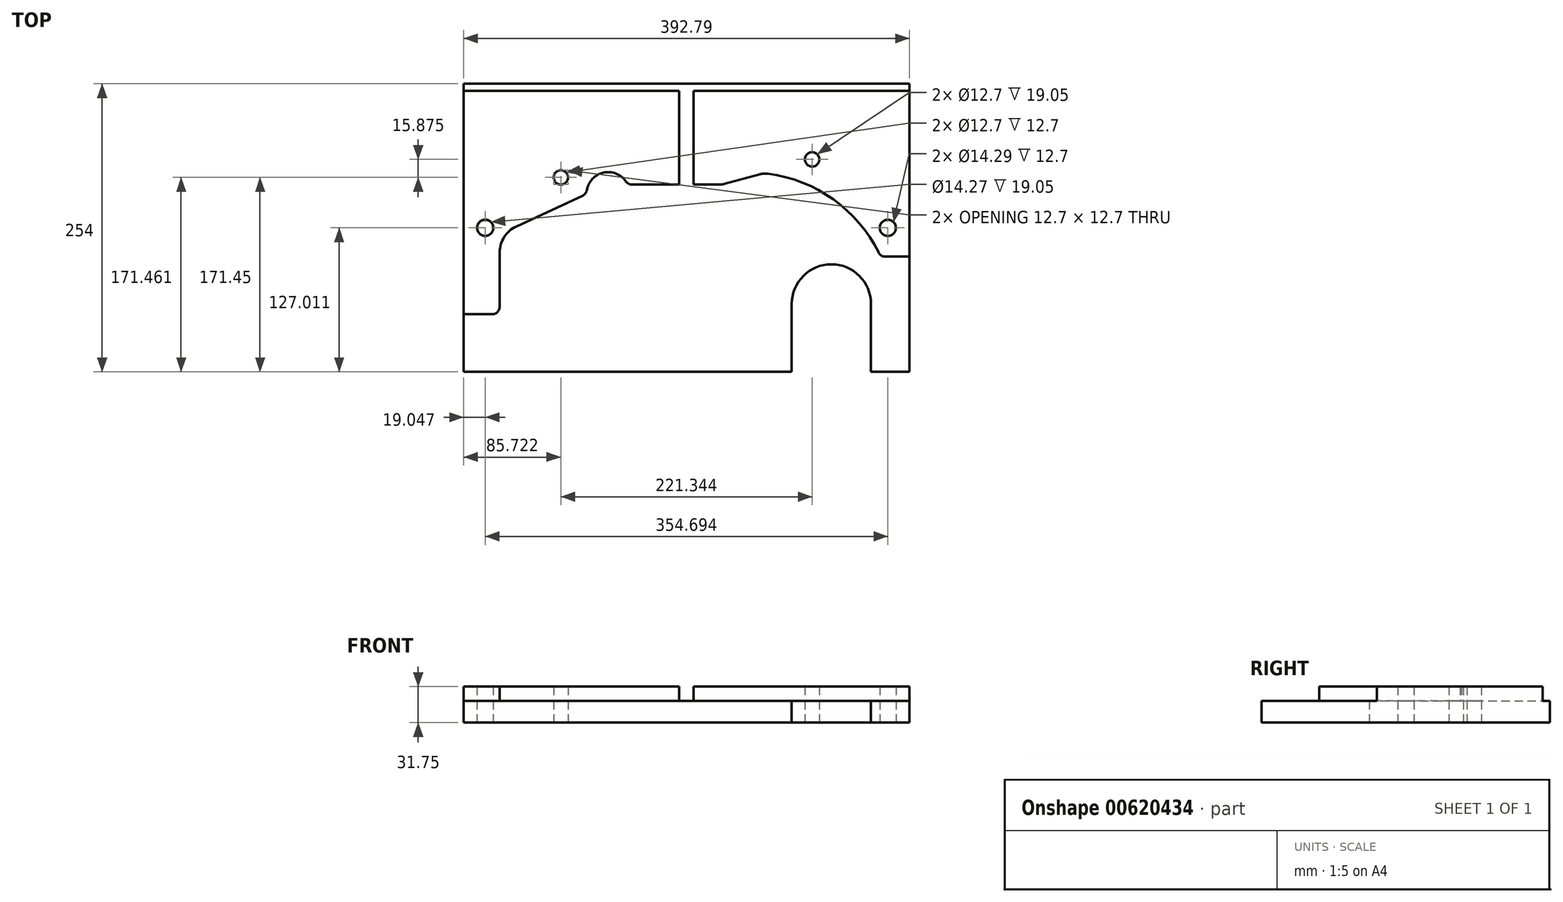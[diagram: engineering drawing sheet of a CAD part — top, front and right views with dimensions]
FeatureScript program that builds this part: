
annotation { "Feature Type Name" : "Feature", "Feature Type Description" : "" }
export const myFeature = defineFeature(function(context is Context, id is Id, definition is map)
    precondition{}
    {
        {
            var Q0;
            Q0=qCreatedBy(makeId("Top.planeOp"),FACE);
            var sketch = newSketch(context, id + "F0", { "sketchPlane" : qUnion([Q0])});
            skLineSegment(sketch, "E0", {"start": v(153.35, -127) * mm, "end": v(-112.4, -127) * mm});
            skArc(sketch, "E1", {"start": v(-112.4, -127) * mm, "mid": v(-149.75, -68.16) * mm, "end": v(-187.1, -127) * mm});
            skLineSegment(sketch, "E2", {"start": v(-187.1, -127) * mm, "end": v(-239.44, -127) * mm});
            skLineSegment(sketch, "E3", {"start": v(-239.44, -127) * mm, "end": v(-239.44, 127) * mm});
            skLineSegment(sketch, "E4", {"start": v(-239.44, 127) * mm, "end": v(153.35, 127) * mm});
            skLineSegment(sketch, "E5", {"start": v(153.35, 127) * mm, "end": v(153.35, -127) * mm});
            skCircle(sketch, "E6", {"center": v(-153.72, 44.45) * mm, "radius": 6.35 * mm});
            skCircle(sketch, "E7", {"center": v(67.63, 60.33) * mm, "radius": 6.35 * mm});
            skCircle(sketch, "E8", {"center": v(-220.4, 0) * mm, "radius": 7.14 * mm});
            skCircle(sketch, "E9", {"center": v(134.3, 0) * mm, "radius": 7.14 * mm});
            skCircle(sketch, "E10", {"center": v(84.58, -67.07) * mm, "radius": 34.93 * mm});
            skSolve(sketch);
        }
        {
            var Q0;
            Q0=qSketchRegion(id+"F0",true);
            extrude(context, id + "F1", {"entities" : qUnion([Q0]), "depth" : 19.05 * mm, "offsetDistance" : 25.4 * mm});
        }
        {
            var Q0;
            Q0=makeQuery(id+"F1.opExtrude","CAP_FACE",FACE,{"disambiguationData":[OSD([sQuery(id+"F0.wireOp",EDGE,"E0"),sQuery(id+"F0.wireOp",EDGE,"E1"),sQuery(id+"F0.wireOp",EDGE,"E2"),sQuery(id+"F0.wireOp",EDGE,"E3"),sQuery(id+"F0.wireOp",EDGE,"E4"),sQuery(id+"F0.wireOp",EDGE,"E5"),sQuery(id+"F0.wireOp",EDGE,"E8"),sQuery(id+"F0.wireOp",EDGE,"E10"),sQuery(id+"F0.wireOp",EDGE,"E9"),sQuery(id+"F0.wireOp",EDGE,"E6"),sQuery(id+"F0.wireOp",EDGE,"E7")])],"isStart":false});
            var sketch = newSketch(context, id + "F2", { "sketchPlane" : qUnion([Q0])});
            skArc(sketch, "E11", {"start": v(-193.03, 1.2) * mm, "mid": v(-203.71, -8.17) * mm, "end": v(-207.7, -21.82) * mm});
            skArc(sketch, "E12", {"start": v(28.82, 47.68) * mm, "mid": v(25.06, 47.8) * mm, "end": v(21.36, 47.17) * mm});
            skLineSegment(sketch, "E13", {"start": v(-9.42, 38.78) * mm, "end": v(21.36, 47.17) * mm});
            skArc(sketch, "E14", {"start": v(-14.43, 38.11) * mm, "mid": v(-11.9, 38.28) * mm, "end": v(-9.42, 38.78) * mm});
            skLineSegment(sketch, "E15", {"start": v(21.36, 47.17) * mm, "end": v(-9.42, 38.78) * mm});
            skArc(sketch, "E16", {"start": v(126.32, -21.97) * mm, "mid": v(86.3, 25.08) * mm, "end": v(28.82, 47.68) * mm});
            skCircle(sketch, "E17", {"center": v(-153.72, 44.46) * mm, "radius": 6.35 * mm});
            skCircle(sketch, "E18", {"center": v(67.63, 60.34) * mm, "radius": 6.35 * mm});
            skCircle(sketch, "E19", {"center": v(-220.4, 0.01) * mm, "radius": 7.14 * mm});
            skCircle(sketch, "E20", {"center": v(134.3, 0.01) * mm, "radius": 7.14 * mm});
            skLineSegment(sketch, "E21", {"start": v(-239.44, 120.66) * mm, "end": v(-49.4, 120.66) * mm});
            skLineSegment(sketch, "E22", {"start": v(-49.4, 120.66) * mm, "end": v(-239.44, 120.66) * mm});
            skLineSegment(sketch, "E23", {"start": v(-49.4, 120.66) * mm, "end": v(-49.4, 38.11) * mm});
            skLineSegment(sketch, "E24", {"start": v(-49.4, 38.11) * mm, "end": v(-49.4, 120.66) * mm});
            skLineSegment(sketch, "E25", {"start": v(-36.7, 38.11) * mm, "end": v(-36.7, 120.66) * mm});
            skLineSegment(sketch, "E26", {"start": v(-36.7, 120.66) * mm, "end": v(-36.7, 38.11) * mm});
            skLineSegment(sketch, "E27", {"start": v(-36.7, 120.66) * mm, "end": v(153.35, 120.66) * mm});
            skLineSegment(sketch, "E28", {"start": v(153.35, 120.66) * mm, "end": v(-36.7, 120.66) * mm});
            skLineSegment(sketch, "E29", {"start": v(-49.4, 38.11) * mm, "end": v(-91.17, 38.11) * mm});
            skLineSegment(sketch, "E30", {"start": v(-91.17, 38.11) * mm, "end": v(-49.4, 38.11) * mm});
            skLineSegment(sketch, "E31", {"start": v(-239.44, -76.19) * mm, "end": v(-239.44, 120.66) * mm});
            skLineSegment(sketch, "E32", {"start": v(-214.04, -76.19) * mm, "end": v(-239.44, -76.19) * mm});
            skArc(sketch, "E33", {"start": v(-214.04, -76.19) * mm, "mid": v(-209.55, -74.33) * mm, "end": v(-207.7, -69.84) * mm});
            skLineSegment(sketch, "E34", {"start": v(-207.7, -21.82) * mm, "end": v(-207.7, -69.84) * mm});
            skArc(sketch, "E35", {"start": v(-193.03, 1.2) * mm, "mid": v(-203.72, -8.17) * mm, "end": v(-207.7, -21.82) * mm});
            skLineSegment(sketch, "E36", {"start": v(-134.46, 28.51) * mm, "end": v(-193.03, 1.2) * mm});
            skArc(sketch, "E37", {"start": v(-134.46, 28.51) * mm, "mid": v(-132.09, 30.42) * mm, "end": v(-130.88, 33.22) * mm});
            skArc(sketch, "E38", {"start": v(-96.4, 40.86) * mm, "mid": v(-116.21, 48.66) * mm, "end": v(-130.88, 33.22) * mm});
            skArc(sketch, "E39", {"start": v(-96.4, 40.86) * mm, "mid": v(-94.12, 38.84) * mm, "end": v(-91.17, 38.11) * mm});
            skLineSegment(sketch, "E40", {"start": v(-239.44, -76.19) * mm, "end": v(-214.04, -76.19) * mm});
            skLineSegment(sketch, "E41", {"start": v(131.96, -25.39) * mm, "end": v(153.35, -25.39) * mm});
            skArc(sketch, "E42", {"start": v(126.27, -21.86) * mm, "mid": v(128.6, -24.44) * mm, "end": v(131.96, -25.39) * mm});
            skArc(sketch, "E43", {"start": v(126.27, -21.86) * mm, "mid": v(86.25, 25.12) * mm, "end": v(28.82, 47.68) * mm});
            skLineSegment(sketch, "E44", {"start": v(-36.7, 38.11) * mm, "end": v(-14.43, 38.11) * mm});
            skLineSegment(sketch, "E45", {"start": v(-193.03, 1.2) * mm, "end": v(-134.46, 28.51) * mm});
            skLineSegment(sketch, "E46", {"start": v(-207.7, -69.84) * mm, "end": v(-207.7, -21.82) * mm});
            skLineSegment(sketch, "E47", {"start": v(-239.44, 120.66) * mm, "end": v(-239.44, -76.19) * mm});
            skLineSegment(sketch, "E48", {"start": v(153.35, -25.39) * mm, "end": v(153.35, 120.66) * mm});
            skLineSegment(sketch, "E49", {"start": v(-14.43, 38.11) * mm, "end": v(-36.7, 38.11) * mm});
            skLineSegment(sketch, "E50", {"start": v(153.35, -25.39) * mm, "end": v(131.96, -25.39) * mm});
            skLineSegment(sketch, "E51", {"start": v(153.35, 120.66) * mm, "end": v(153.35, -25.39) * mm});
            skSolve(sketch);
        }
        {
            var Q0;
            Q0=qSketchRegion(id+"F2",true);
            extrude(context, id + "F3", {"entities" : qUnion([Q0]), "operationType" : NewBodyOperationType.ADD, "depth" : 12.7 * mm, "offsetDistance" : 25.4 * mm});
        }
        {
            var Q0;
            {var subQ0=sQuery(id+"F0.wireOp",EDGE,"E2");var subQ1=sQuery(id+"F0.wireOp",EDGE,"E1");var subQ2=sQuery(id+"F0.wireOp",EDGE,"E3");var subQ3=sQuery(id+"F0.wireOp",EDGE,"E0");var subQ4=sQuery(id+"F0.wireOp",EDGE,"E4");var subQ5=sQuery(id+"F0.wireOp",EDGE,"E5");var subQ6=sQuery(id+"F0.wireOp",EDGE,"E10");Q0=makeQuery(id+"F3.boolean.opBoolean","SPLIT",FACE,{"disambiguationData":[TD([makeQuery(id+"F1.opExtrude","SWEPT_FACE",FACE,{"disambiguationData":[OSD([subQ3])]})])],"derivedFrom":makeQuery(id+"F1.opExtrude","CAP_FACE",FACE,{"disambiguationData":[OSD([subQ3,subQ1,subQ0,subQ2,subQ4,subQ5,sQuery(id+"F0.wireOp",EDGE,"E8"),subQ6,sQuery(id+"F0.wireOp",EDGE,"E9"),sQuery(id+"F0.wireOp",EDGE,"E6"),sQuery(id+"F0.wireOp",EDGE,"E7")])],"isStart":false})});}
            var sketch = newSketch(context, id + "F4", { "sketchPlane" : qUnion([Q0])});
            skCircle(sketch, "E52", {"center": v(84.58, -67.07) * mm, "radius": 34.93 * mm});
            skLineSegment(sketch, "E53", {"start": v(119.5, -127) * mm, "end": v(119.5, -67.07) * mm});
            skLineSegment(sketch, "E54", {"start": v(49.65, -127) * mm, "end": v(49.65, -67.07) * mm});
            skLineSegment(sketch, "E55", {"start": v(49.65, -127) * mm, "end": v(119.5, -127) * mm});
            skSolve(sketch);
        }
        {
            var Q0;
            Q0=qSketchRegion(id+"F4",true);
            extrude(context, id + "F5", {"entities" : qUnion([Q0]), "operationType" : NewBodyOperationType.REMOVE, "oppositeDirection" : true, "depth" : 25.4 * mm, "offsetDistance" : 25.4 * mm});
        }
        {
            var Q0;
            {var subQ0=sQuery(id+"F0.wireOp",EDGE,"E2");var subQ1=sQuery(id+"F0.wireOp",EDGE,"E1");var subQ2=sQuery(id+"F0.wireOp",EDGE,"E3");var subQ3=sQuery(id+"F0.wireOp",EDGE,"E0");var subQ4=sQuery(id+"F0.wireOp",EDGE,"E4");var subQ5=sQuery(id+"F0.wireOp",EDGE,"E5");var subQ6=sQuery(id+"F0.wireOp",EDGE,"E10");Q0=makeQuery(id+"F3.boolean.opBoolean","SPLIT",FACE,{"disambiguationData":[TD([makeQuery(id+"F1.opExtrude","SWEPT_FACE",FACE,{"disambiguationData":[OSD([subQ3])]})])],"derivedFrom":makeQuery(id+"F1.opExtrude","CAP_FACE",FACE,{"disambiguationData":[OSD([subQ3,subQ1,subQ0,subQ2,subQ4,subQ5,sQuery(id+"F0.wireOp",EDGE,"E8"),subQ6,sQuery(id+"F0.wireOp",EDGE,"E9"),sQuery(id+"F0.wireOp",EDGE,"E6"),sQuery(id+"F0.wireOp",EDGE,"E7")])],"isStart":false})});}
            var sketch = newSketch(context, id + "F6", { "sketchPlane" : qUnion([Q0])});
            skArc(sketch, "E56", {"start": v(-108.47, -109.44) * mm, "mid": v(-149.75, -68.16) * mm, "end": v(-191.02, -109.44) * mm});
            skLineSegment(sketch, "E57", {"start": v(-108.47, -127) * mm, "end": v(-108.47, -109.44) * mm});
            skLineSegment(sketch, "E58", {"start": v(-191.02, -127) * mm, "end": v(-191.02, -109.44) * mm});
            skLineSegment(sketch, "E59", {"start": v(-191.02, -127) * mm, "end": v(-108.47, -127) * mm});
            skSolve(sketch);
        }
        {
            var Q0;
            Q0=qSketchRegion(id+"F6",true);
            extrude(context, id + "F7", {"entities" : qUnion([Q0]), "operationType" : NewBodyOperationType.REMOVE, "oppositeDirection" : true, "depth" : 25.4 * mm, "offsetDistance" : 25.4 * mm});
        }
        {
            var Q0;
            {var subQ0=sQuery(id+"F0.wireOp",EDGE,"E2");var subQ1=sQuery(id+"F0.wireOp",EDGE,"E1");var subQ2=sQuery(id+"F0.wireOp",EDGE,"E3");var subQ3=sQuery(id+"F0.wireOp",EDGE,"E0");var subQ4=sQuery(id+"F0.wireOp",EDGE,"E4");var subQ5=sQuery(id+"F0.wireOp",EDGE,"E5");var subQ6=sQuery(id+"F0.wireOp",EDGE,"E10");Q0=makeQuery(id+"F3.boolean.opBoolean","SPLIT",FACE,{"disambiguationData":[TD([makeQuery(id+"F1.opExtrude","SWEPT_FACE",FACE,{"disambiguationData":[OSD([subQ3])]})])],"derivedFrom":makeQuery(id+"F1.opExtrude","CAP_FACE",FACE,{"disambiguationData":[OSD([subQ3,subQ1,subQ0,subQ2,subQ4,subQ5,sQuery(id+"F0.wireOp",EDGE,"E8"),subQ6,sQuery(id+"F0.wireOp",EDGE,"E9"),sQuery(id+"F0.wireOp",EDGE,"E6"),sQuery(id+"F0.wireOp",EDGE,"E7")])],"isStart":false})});}
            var sketch = newSketch(context, id + "F8", { "sketchPlane" : qUnion([Q0])});
            skArc(sketch, "E60.0", {"start": v(-108.47, -109.44) * mm, "mid": v(-149.75, -68.16) * mm, "end": v(-191.02, -109.44) * mm});
            skPoint(sketch, "E61.0", {"position": v(-191.02, -118.22) * mm});
            skLineSegment(sketch, "E62.0", {"start": v(-191.02, -127) * mm, "end": v(-191.02, -109.44) * mm});
            skLineSegment(sketch, "E63.0", {"start": v(-108.47, -127) * mm, "end": v(-108.47, -109.44) * mm});
            skLineSegment(sketch, "E64", {"start": v(-191.02, -127) * mm, "end": v(-108.47, -127) * mm});
            skSolve(sketch);
        }
        {
            var Q0;
            Q0 = qSketchRegion(id + "F8", true);
            extrude(context, id + "F9", {"entities" : qUnion([Q0]), "operationType" : NewBodyOperationType.ADD, "oppositeDirection" : true, "depth" : 19.05 * mm, "offsetDistance" : 25.4 * mm});
        }
    });
